# Revit family: HERZ-Mini-GS-Design-Thermostatic Sensor M28x1.5 9200 06
name_source: partatom
category: Rohrzubehör
revit_build: Autodesk Revit 2018 (Build: 20190510_1515(x64)
units: mm (PartAtom-declared; Revit-internal decimal feet)

## family parameters
Arbeitsebenenbasiert = Nein
Beim Laden mit Abzugskörper schneiden = Nein
Bemaßung runder Anschluss = Durchmesser verwenden
Gemeinsam genutzt = Nein
Immer vertikal = Nein
OmniClass-Nummer = 23.65.55.14
OmniClass-Titel = Valves for Liquid Services
Teiletyp = Normal

## types (1)
- HERZ-Mini-GS-Design-Thermostatic Sensor M28x1.5 9200 06
    Application = For mounting on valves that are designed for thermostatic operation.
    Frost protection = 6 °C
    Frost protection * = When set to *, the valve automatically opens at approx.
6 ° C ambient temperature and prevents the system from freezing.
    Frost protection setpoint range = 6-28°C
    Hand wheel = plastic, white
    Hersteller = HERZ Armaturen Ges.m.b.H.
    Operation = The HERZ thermostat serves as a sensing and control element.
The volumetric change of the liquid filling in the HERZ hydrosensor moves the thrust spindle of the valve.
    Part number = 1920006
    S01 = 73 mm  [stored 0.239501 ft]
    S02 = 60 mm  [stored 0.19685 ft]
    Set value range = 6-28°C
    Shut off zero position = When set to "0", the thermostatic valve is shut off and the frost protection is disabled.
    URL = www.herzvalves.com

note: [stored X ft] marks values corroborated as IEEE doubles in the binary element streams (Revit-internal decimal feet)
